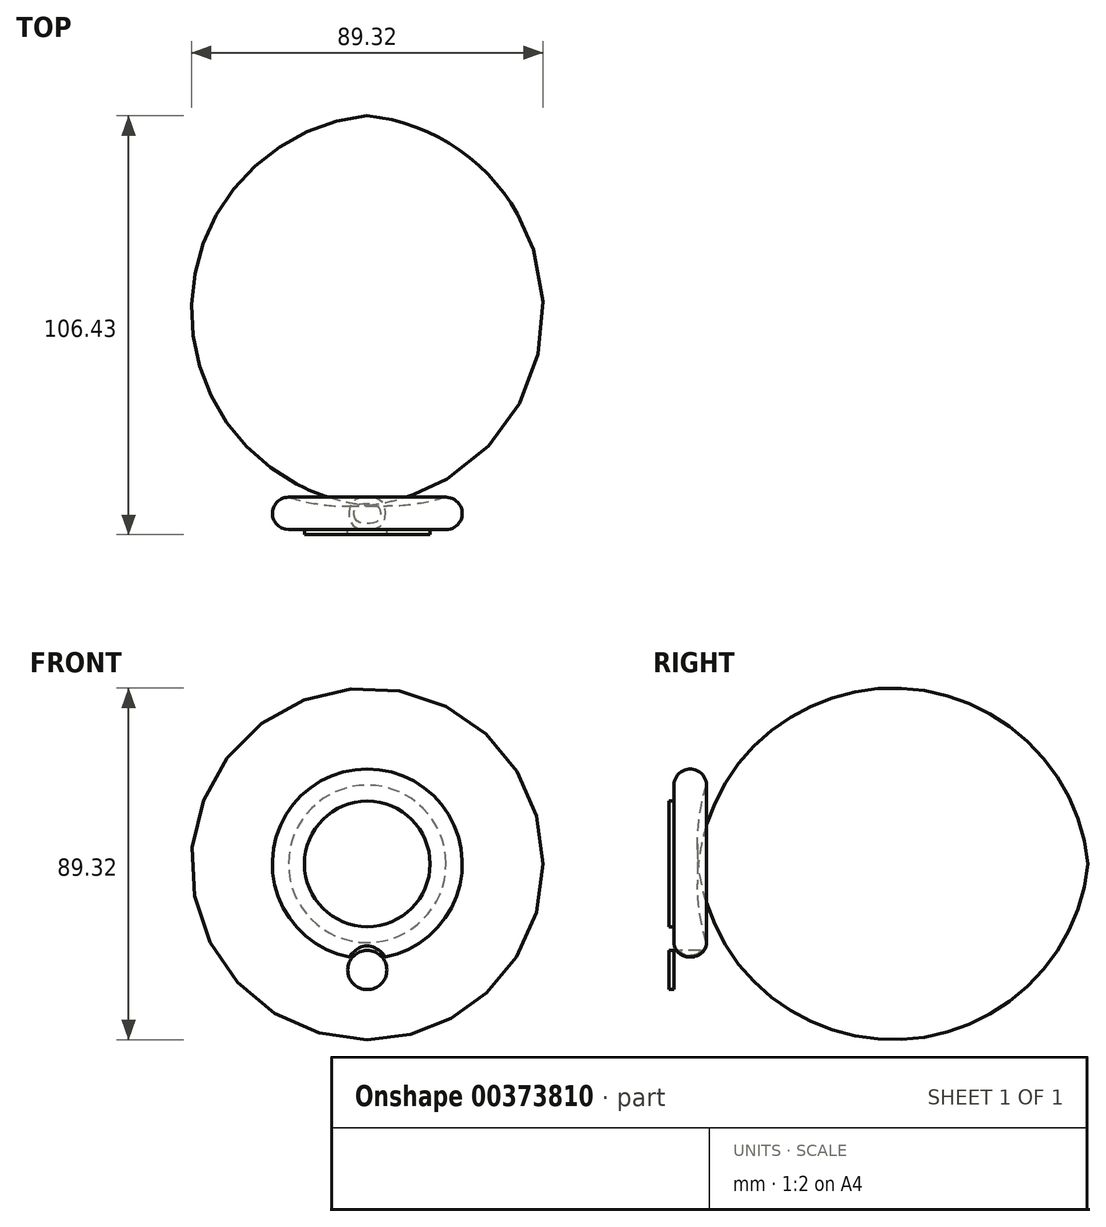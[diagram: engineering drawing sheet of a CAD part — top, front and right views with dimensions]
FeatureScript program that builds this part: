
annotation { "Feature Type Name" : "Feature", "Feature Type Description" : "" }
export const myFeature = defineFeature(function(context is Context, id is Id, definition is map)
    precondition{}
    {
        {
            var Q0;
            Q0=qCreatedBy(makeId("Top.planeOp"),FACE);
            var sketch = newSketch(context, id + "F0", { "sketchPlane" : qUnion([Q0])});
            skLineSegment(sketch, "E0", {"start": v(0, 0) * mm, "end": v(-20, 0) * mm});
            skArc(sketch, "E1", {"start": v(-20, 8.24) * mm, "mid": v(-24.12, 4.12) * mm, "end": v(-20, 0) * mm});
            skArc(sketch, "E2", {"start": v(-20, 8.24) * mm, "mid": v(-10.1, 6.2) * mm, "end": v(0, 6.2) * mm});
            skLineSegment(sketch, "E3", {"start": v(0, 6.2) * mm, "end": v(0, 0) * mm});
            skSolve(sketch);
        }
        {
            var Q0;
            Q0=makeQuery(id+"F0.imprint","IMPRINT",FACE,{"disambiguationData":[TD([[makeQuery(id+"F0.imprint","IMPRINT",EDGE,{"derivedFrom":sQuery(id+"F0.wireOp",EDGE,"E0")}),-1.0]])]});
            var Q1;
            Q1=sQuery(id+"F0.wireOp",EDGE,"E3");
            revolve(context, id + "F1", {"entities" : qUnion([Q0]), "axis" : qUnion([Q1]), "revolveType" : RevolveType.FULL});
        }
        {
            var Q0;
            Q0=qCreatedBy(makeId("Front.planeOp"),FACE);
            var sketch = newSketch(context, id + "F2", { "sketchPlane" : qUnion([Q0])});
            skCircle(sketch, "E4", {"center": v(0, -26.97) * mm, "radius": 4.97 * mm});
            skCircle(sketch, "E5", {"center": v(0, 0) * mm, "radius": 15.95 * mm});
            skSolve(sketch);
        }
        {
            var Q0;
            Q0=makeQuery(id+"F2.imprint","IMPRINT",FACE,{"disambiguationData":[TD([[makeQuery(id+"F2.imprint","IMPRINT",EDGE,{"derivedFrom":sQuery(id+"F2.wireOp",EDGE,"E4")}),1.0]])]});
            extrude(context, id + "F3", {"entities" : qUnion([Q0]), "operationType" : NewBodyOperationType.REMOVE, "oppositeDirection" : true, "depth" : 25.4 * mm});
        }
        {
            var Q0;
            Q0=makeQuery(id+"F3.boolean.opBoolean","INTERSECT",EDGE,{"derivedFrom":[makeQuery(id+"F1.opRevolve","SWEPT_FACE",FACE,{"disambiguationData":[OSD([sQuery(id+"F0.wireOp",EDGE,"E1")])]}),makeQuery(id+"F3.opExtrude","SWEPT_FACE",FACE,{"disambiguationData":[OSD([sQuery(id+"F2.wireOp",EDGE,"E4")])]})]});
            fillet(context, id + "F4", {"entities" : qUnion([Q0]), "radius" : 1.5 * mm, "tangentPropagation" : true, "allowEdgeOverflow" : false});
        }
        {
            var Q0;
            Q0 = qSketchRegion(id + "F2", true);
            extrude(context, id + "F5", {"entities" : qUnion([Q0]), "operationType" : NewBodyOperationType.ADD, "depth" : 1.27 * mm});
        }
    });
